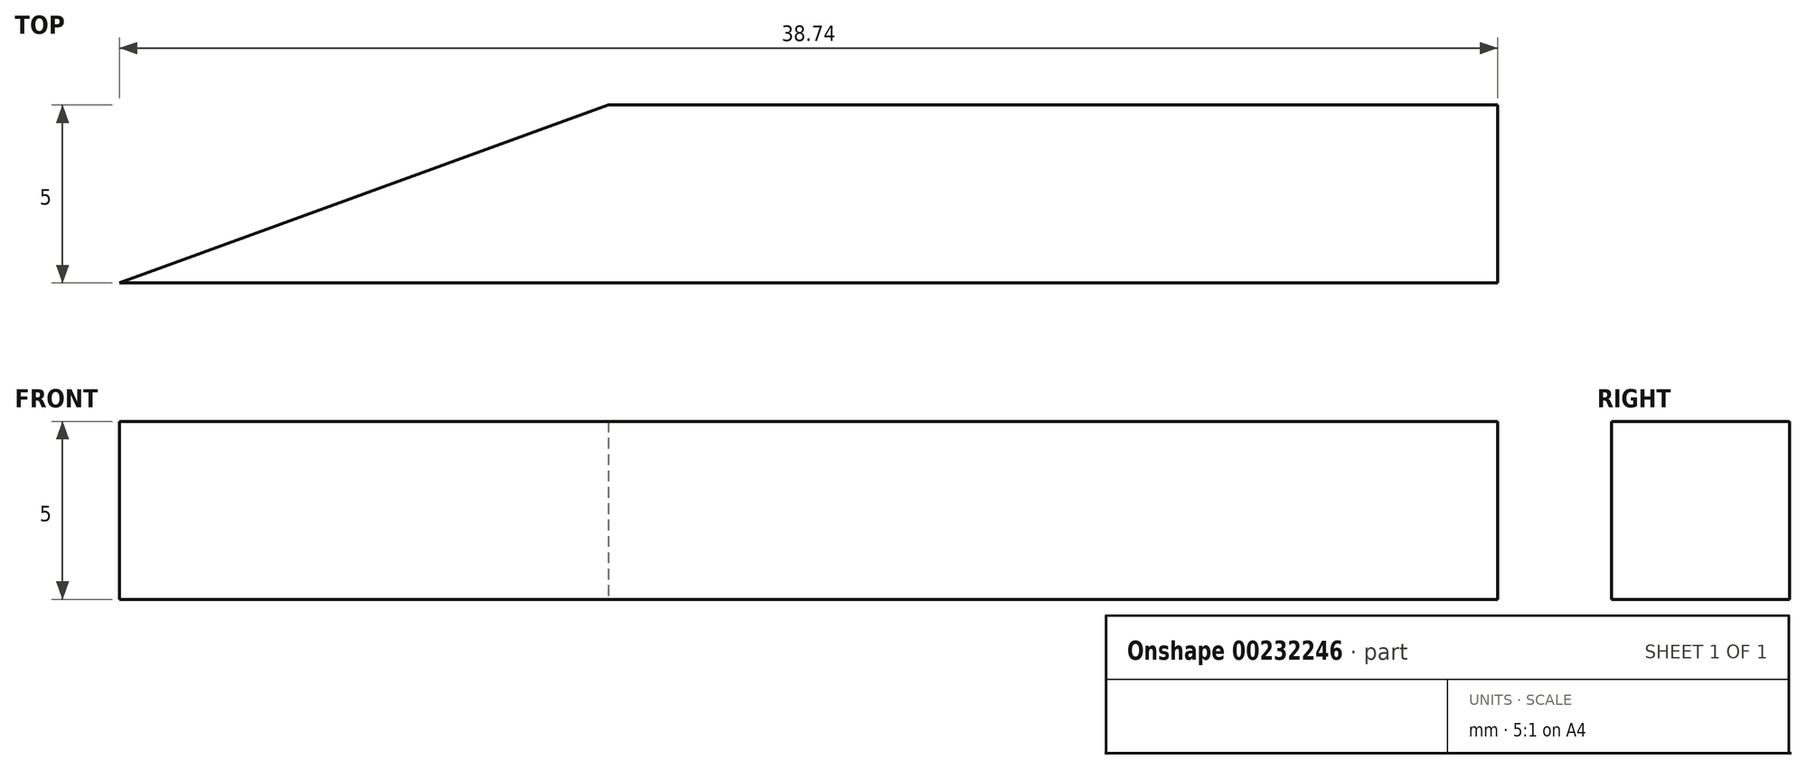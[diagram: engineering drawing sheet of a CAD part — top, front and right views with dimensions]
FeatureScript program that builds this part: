
annotation { "Feature Type Name" : "Feature", "Feature Type Description" : "" }
export const myFeature = defineFeature(function(context is Context, id is Id, definition is map)
    precondition{}
    {
        {
            var Q0;
            Q0=qCreatedBy(makeId("Top.planeOp"),FACE);
            var sketch = newSketch(context, id + "F0", { "sketchPlane" : qUnion([Q0])});
            skLineSegment(sketch, "E0.bottom", {"start": v(0.31, 0.84) * mm, "end": v(25.31, 0.84) * mm});
            skLineSegment(sketch, "E0.top", {"start": v(-13.43, -4.16) * mm, "end": v(25.31, -4.16) * mm});
            skLineSegment(sketch, "E0.right", {"start": v(25.31, 0.84) * mm, "end": v(25.31, -4.16) * mm});
            skPoint(sketch, "E1", {"position": v(0.31, 0.84) * mm});
            skLineSegment(sketch, "E2", {"start": v(-13.43, -4.16) * mm, "end": v(0.31, 0.84) * mm});
            skSolve(sketch);
        }
        {
            var Q0;
            Q0 = qSketchRegion(id + "F0", true);
            extrude(context, id + "F1", {"entities" : qUnion([Q0]), "depth" : 5 * mm});
        }
    });
